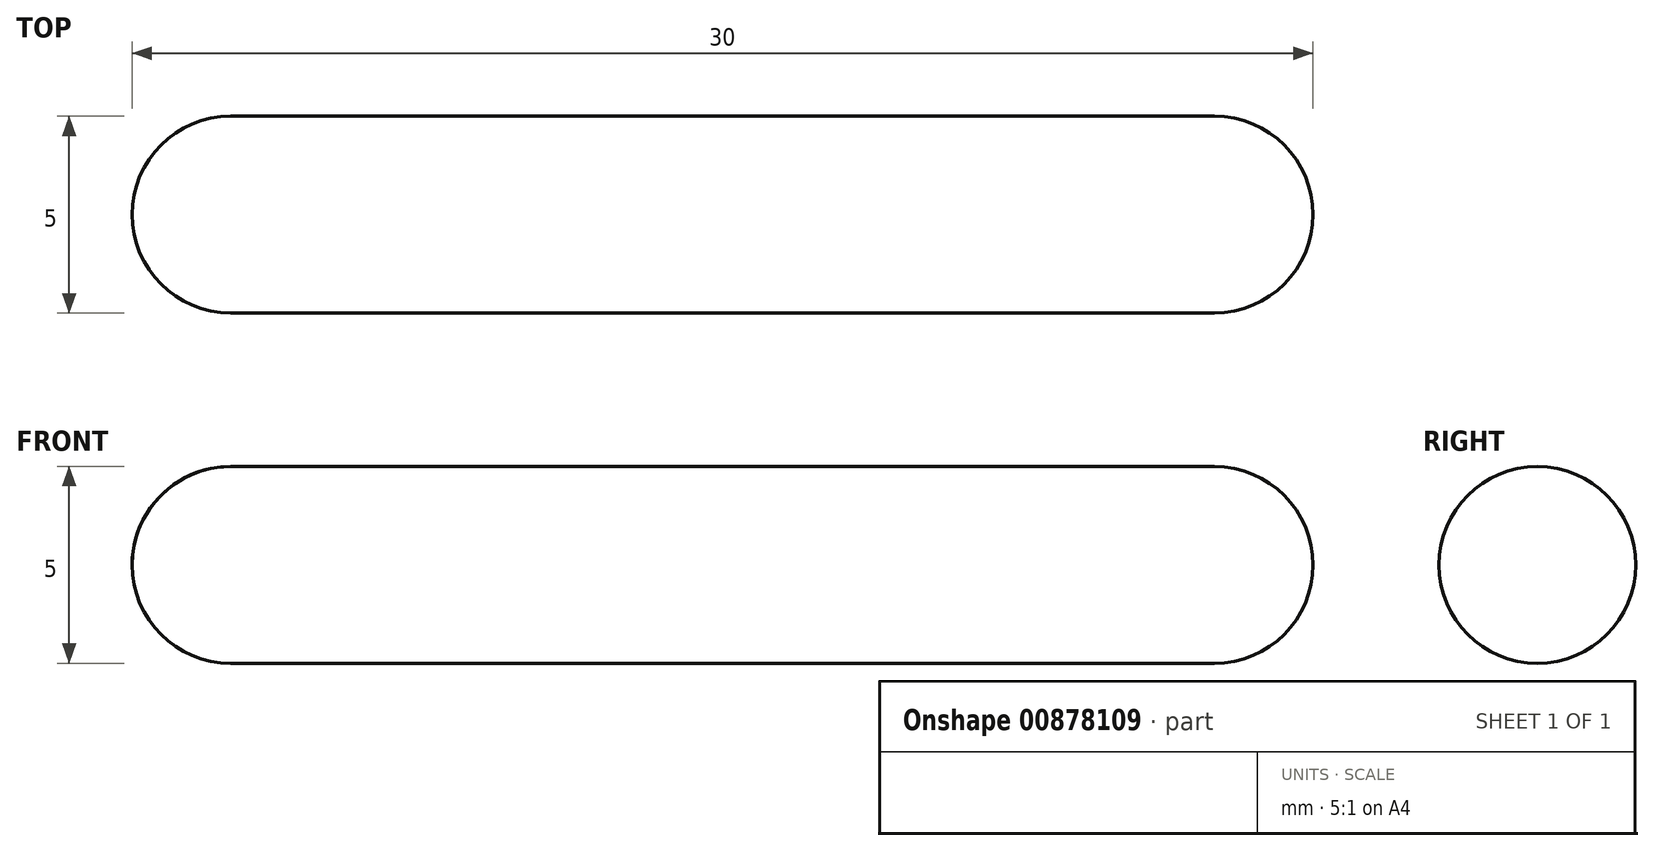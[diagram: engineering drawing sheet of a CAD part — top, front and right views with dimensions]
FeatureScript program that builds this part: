
annotation { "Feature Type Name" : "Feature", "Feature Type Description" : "" }
export const myFeature = defineFeature(function(context is Context, id is Id, definition is map)
    precondition{}
    {
        {
            var Q0;
            Q0=qCreatedBy(makeId("Top.planeOp"),FACE);
            var sketch = newSketch(context, id + "F0", { "sketchPlane" : qUnion([Q0])});
            skLineSegment(sketch, "E0.bottom", {"start": v(15, 2.5) * mm, "end": v(-15, 2.5) * mm});
            skLineSegment(sketch, "E0.top", {"start": v(15, -2.5) * mm, "end": v(-15, -2.5) * mm});
            skLineSegment(sketch, "E0.left", {"start": v(15, 2.5) * mm, "end": v(15, -2.5) * mm});
            skLineSegment(sketch, "E0.right", {"start": v(-15, 2.5) * mm, "end": v(-15, -2.5) * mm});
            skPoint(sketch, "E0.middle", {"position": v(0, 0) * mm});
            skSolve(sketch);
        }
        {
            var Q0;
            Q0 = qSketchRegion(id + "F0", true);
            extrude(context, id + "F1", {"entities" : qUnion([Q0]), "depth" : 5 * mm, "offsetDistance" : 25 * mm});
        }
        {
            var Q0;
            Q0=makeQuery(id+"F1.opExtrude","CAP_EDGE",EDGE,{"disambiguationData":[OSD([sQuery(id+"F0.wireOp",EDGE,"E0.top")])],"isStart":false});
            var Q1;
            Q1=makeQuery(id+"F1.opExtrude","CAP_EDGE",EDGE,{"disambiguationData":[OSD([sQuery(id+"F0.wireOp",EDGE,"E0.bottom")])],"isStart":false});
            var Q2;
            Q2=makeQuery(id+"F1.opExtrude","CAP_EDGE",EDGE,{"disambiguationData":[OSD([sQuery(id+"F0.wireOp",EDGE,"E0.left")])],"isStart":false});
            var Q3;
            Q3=makeQuery(id+"F1.opExtrude","CAP_EDGE",EDGE,{"disambiguationData":[OSD([sQuery(id+"F0.wireOp",EDGE,"E0.left")])],"isStart":true});
            var Q4;
            Q4=makeQuery(id+"F1.opExtrude","SWEPT_EDGE",EDGE,{"disambiguationData":[OSD([sQuery(id+"F0.wireOp",EDGE,"E0.top"),sQuery(id+"F0.wireOp",EDGE,"E0.left")])]});
            var Q5;
            Q5=makeQuery(id+"F1.opExtrude","CAP_EDGE",EDGE,{"disambiguationData":[OSD([sQuery(id+"F0.wireOp",EDGE,"E0.right")])],"isStart":false});
            var Q6;
            Q6=makeQuery(id+"F1.opExtrude","CAP_EDGE",EDGE,{"disambiguationData":[OSD([sQuery(id+"F0.wireOp",EDGE,"E0.top")])],"isStart":true});
            var Q7;
            Q7=makeQuery(id+"F1.opExtrude","SWEPT_EDGE",EDGE,{"disambiguationData":[OSD([sQuery(id+"F0.wireOp",EDGE,"E0.top"),sQuery(id+"F0.wireOp",EDGE,"E0.right")])]});
            var Q8;
            Q8=makeQuery(id+"F1.opExtrude","CAP_EDGE",EDGE,{"disambiguationData":[OSD([sQuery(id+"F0.wireOp",EDGE,"E0.right")])],"isStart":true});
            var Q9;
            Q9=makeQuery(id+"F1.opExtrude","SWEPT_EDGE",EDGE,{"disambiguationData":[OSD([sQuery(id+"F0.wireOp",EDGE,"E0.bottom"),sQuery(id+"F0.wireOp",EDGE,"E0.right")])]});
            var Q10;
            Q10=makeQuery(id+"F1.opExtrude","CAP_EDGE",EDGE,{"disambiguationData":[OSD([sQuery(id+"F0.wireOp",EDGE,"E0.bottom")])],"isStart":true});
            var Q11;
            Q11=makeQuery(id+"F1.opExtrude","SWEPT_EDGE",EDGE,{"disambiguationData":[OSD([sQuery(id+"F0.wireOp",EDGE,"E0.bottom"),sQuery(id+"F0.wireOp",EDGE,"E0.left")])]});
            fillet(context, id + "F2", {"entities" : qUnion([Q0, Q1, Q2, Q3, Q4, Q5, Q6, Q7, Q8, Q9, Q10, Q11]), "radius" : 2.5 * mm, "tangentPropagation" : true, "allowEdgeOverflow" : false});
        }
    });
